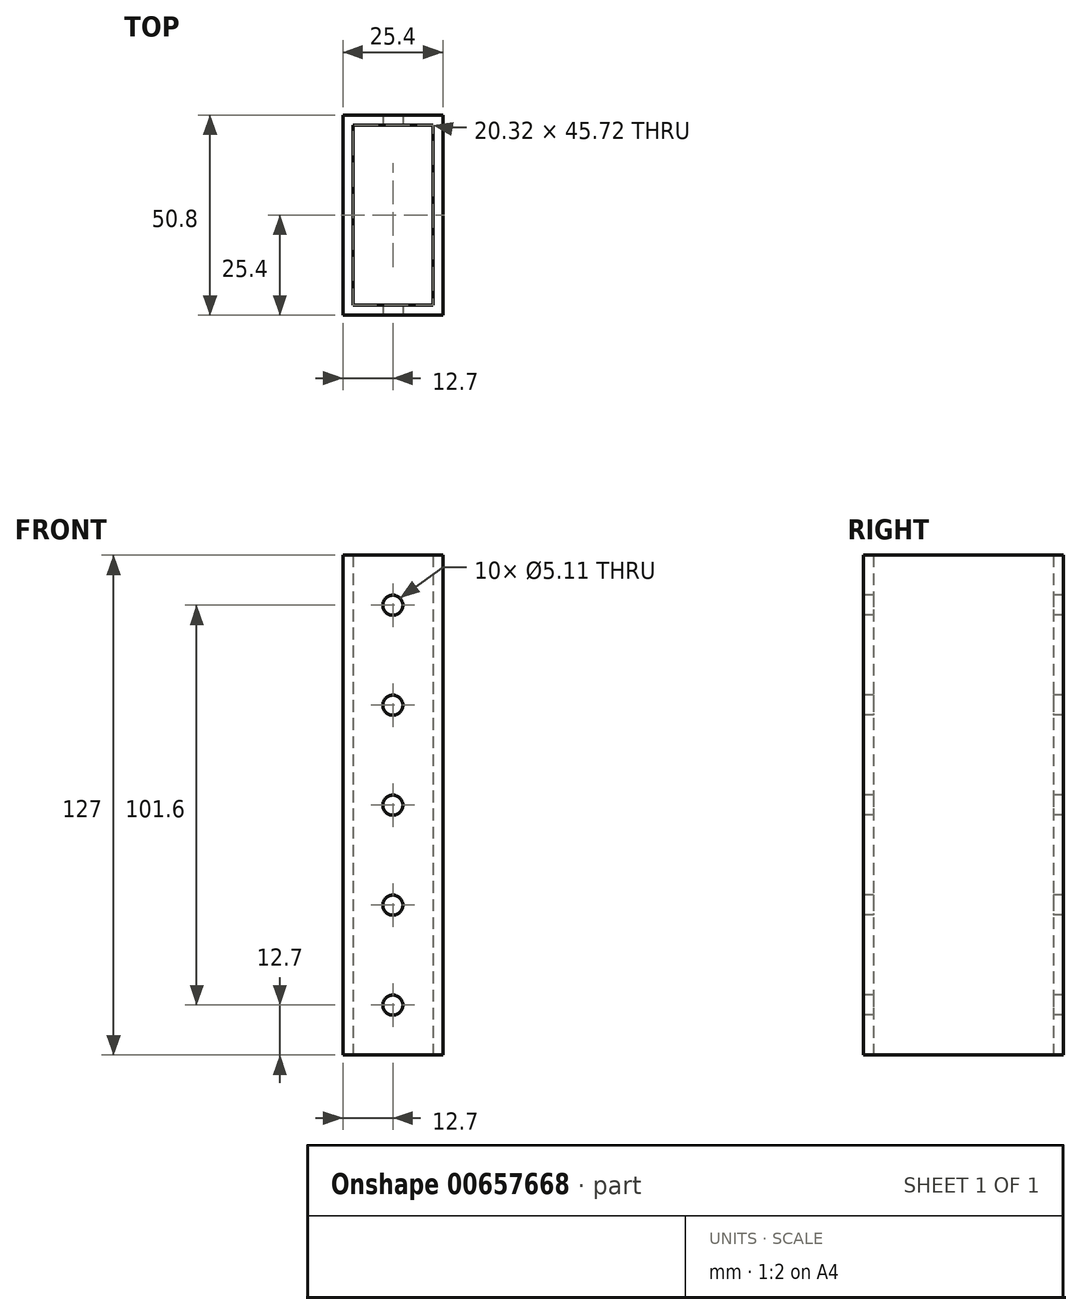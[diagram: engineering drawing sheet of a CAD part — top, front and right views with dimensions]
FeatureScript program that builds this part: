
annotation { "Feature Type Name" : "Feature", "Feature Type Description" : "" }
export const myFeature = defineFeature(function(context is Context, id is Id, definition is map)
    precondition{}
    {
        {
            var Q0;
            Q0=qCreatedBy(makeId("Top.planeOp"),FACE);
            var sketch = newSketch(context, id + "F0", { "sketchPlane" : qUnion([Q0])});
            skLineSegment(sketch, "E0.bottom", {"start": v(0, 0) * mm, "end": v(25.4, 0) * mm});
            skLineSegment(sketch, "E0.top", {"start": v(0, -50.8) * mm, "end": v(25.4, -50.8) * mm});
            skLineSegment(sketch, "E0.left", {"start": v(0, 0) * mm, "end": v(0, -50.8) * mm});
            skLineSegment(sketch, "E0.right", {"start": v(25.4, 0) * mm, "end": v(25.4, -50.8) * mm});
            skLineSegment(sketch, "E1.bottom", {"start": v(2.54, -2.54) * mm, "end": v(22.86, -2.54) * mm});
            skLineSegment(sketch, "E1.top", {"start": v(2.54, -48.26) * mm, "end": v(22.86, -48.26) * mm});
            skLineSegment(sketch, "E1.left", {"start": v(2.54, -2.54) * mm, "end": v(2.54, -48.26) * mm});
            skLineSegment(sketch, "E1.right", {"start": v(22.86, -2.54) * mm, "end": v(22.86, -48.26) * mm});
            skSolve(sketch);
        }
        {
            var Q0;
            Q0=makeQuery(id+"F0.imprint","IMPRINT",FACE,{"disambiguationData":[TD([[makeQuery(id+"F0.imprint","IMPRINT",EDGE,{"derivedFrom":sQuery(id+"F0.wireOp",EDGE,"E0.bottom")}),-1.0]])]});
            extrude(context, id + "F1", {"entities" : qUnion([Q0]), "depth" : 127 * mm, "offsetDistance" : 25.4 * mm});
        }
        {
            var Q0;
            Q0=makeQuery(id+"F1.opExtrude","SWEPT_FACE",FACE,{"disambiguationData":[OSD([sQuery(id+"F0.wireOp",EDGE,"E0.top")])]});
            var sketch = newSketch(context, id + "F2", { "sketchPlane" : qUnion([Q0])});
            skCircle(sketch, "E2", {"center": v(12.7, 12.7) * mm, "radius": 2.55 * mm});
            skCircle(sketch, "E3.0.1.0", {"center": v(12.7, 38.1) * mm, "radius": 2.55 * mm});
            skCircle(sketch, "E3.0.2.0", {"center": v(12.7, 63.5) * mm, "radius": 2.55 * mm});
            skCircle(sketch, "E3.0.3.0", {"center": v(12.7, 88.9) * mm, "radius": 2.55 * mm});
            skLineSegment(sketch, "E3.direction1", {"start": v(12.7, 12.7) * mm, "end": v(38.1, 12.7) * mm, "construction": true});
            skLineSegment(sketch, "E3.direction2", {"start": v(12.7, 12.7) * mm, "end": v(12.7, 38.1) * mm, "construction": true});
            skCircle(sketch, "E4.0.0.4", {"center": v(12.7, 114.3) * mm, "radius": 2.55 * mm});
            skCircle(sketch, "E4.0.0.5", {"center": v(12.7, 139.7) * mm, "radius": 2.55 * mm});
            skSolve(sketch);
        }
        {
            var Q0;
            Q0=makeQuery(id+"F2.imprint","IMPRINT",FACE,{"disambiguationData":[TD([[makeQuery(id+"F2.imprint","IMPRINT",EDGE,{"derivedFrom":sQuery(id+"F2.wireOp",EDGE,"E3.0.3.0")}),1.0]])]});
            var Q1;
            Q1=makeQuery(id+"F2.imprint","IMPRINT",FACE,{"disambiguationData":[TD([[makeQuery(id+"F2.imprint","IMPRINT",EDGE,{"derivedFrom":sQuery(id+"F2.wireOp",EDGE,"E3.0.2.0")}),1.0]])]});
            var Q2;
            Q2=makeQuery(id+"F2.imprint","IMPRINT",FACE,{"disambiguationData":[TD([[makeQuery(id+"F2.imprint","IMPRINT",EDGE,{"derivedFrom":sQuery(id+"F2.wireOp",EDGE,"E3.0.1.0")}),1.0]])]});
            var Q3;
            Q3=makeQuery(id+"F2.imprint","IMPRINT",FACE,{"disambiguationData":[TD([[makeQuery(id+"F2.imprint","IMPRINT",EDGE,{"derivedFrom":sQuery(id+"F2.wireOp",EDGE,"E2")}),1.0]])]});
            var Q4;
            Q4=makeQuery(id+"F2.imprint","IMPRINT",FACE,{"disambiguationData":[TD([[makeQuery(id+"F2.imprint","IMPRINT",EDGE,{"derivedFrom":sQuery(id+"F2.wireOp",EDGE,"E4.0.0.4")}),1.0]])]});
            var Q5;
            Q5=makeQuery(id+"F2.imprint","IMPRINT",FACE,{"disambiguationData":[TD([[makeQuery(id+"F2.imprint","IMPRINT",EDGE,{"derivedFrom":sQuery(id+"F2.wireOp",EDGE,"E4.0.0.5")}),1.0]])]});
            extrude(context, id + "F3", {"entities" : qUnion([Q0, Q1, Q2, Q3, Q4, Q5]), "operationType" : NewBodyOperationType.REMOVE, "oppositeDirection" : true, "depth" : 76.2 * mm, "offsetDistance" : 25.4 * mm});
        }
    });
